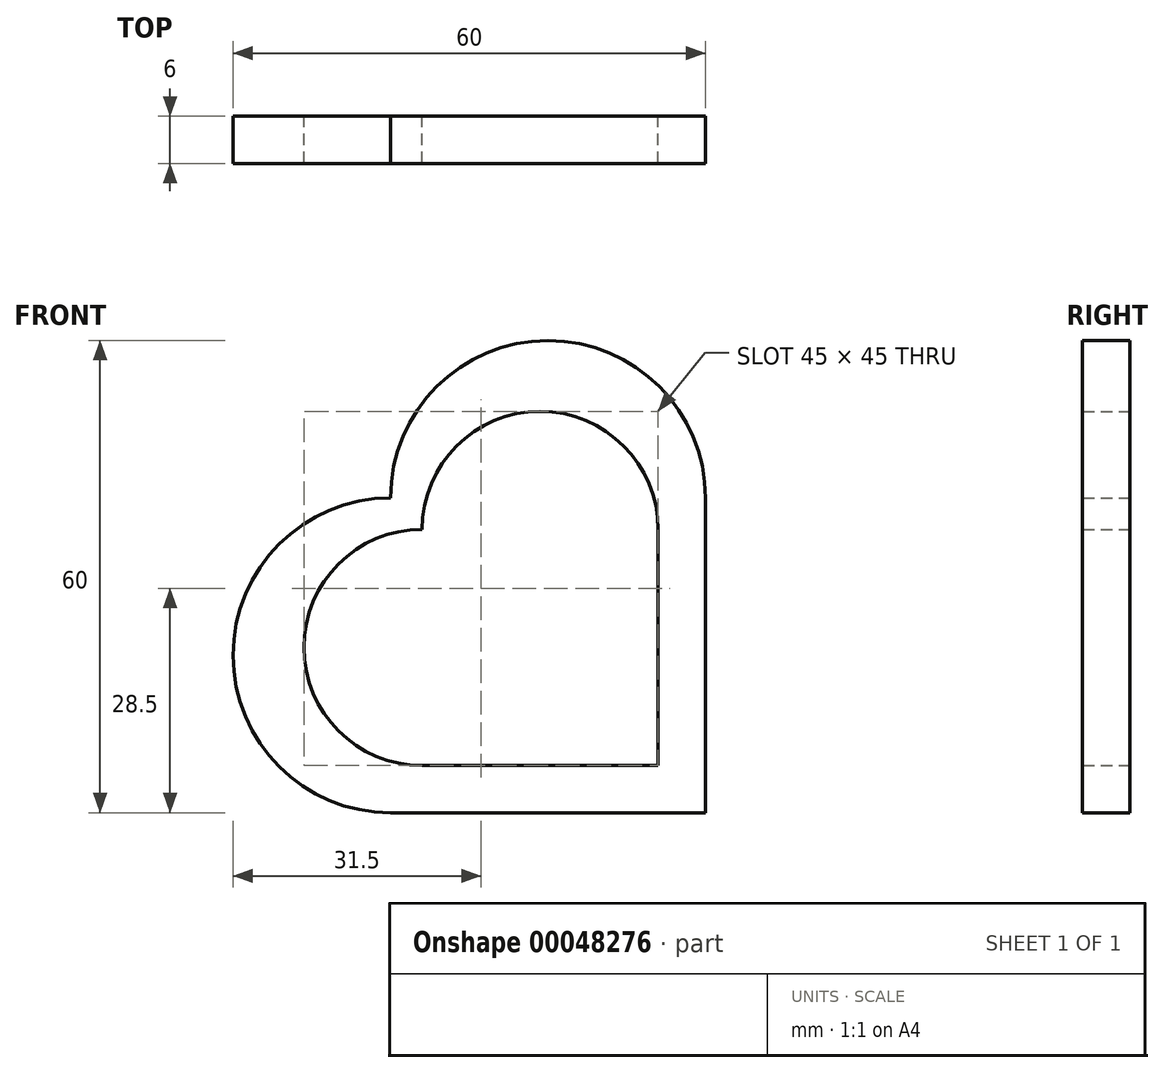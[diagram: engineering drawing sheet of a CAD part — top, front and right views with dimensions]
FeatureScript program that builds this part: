
annotation { "Feature Type Name" : "Feature", "Feature Type Description" : "" }
export const myFeature = defineFeature(function(context is Context, id is Id, definition is map)
    precondition{}
    {
        {
            var Q0;
            Q0=qCreatedBy(makeId("Front.planeOp"),FACE);
            var sketch = newSketch(context, id + "F0", { "sketchPlane" : qUnion([Q0])});
            skLineSegment(sketch, "E0", {"start": v(0, 0) * mm, "end": v(-40, 0) * mm});
            skLineSegment(sketch, "E1", {"start": v(0, 40) * mm, "end": v(0, 0) * mm});
            skArc(sketch, "E2", {"start": v(-40, 40) * mm, "mid": v(-60, 20) * mm, "end": v(-40, 0) * mm});
            skArc(sketch, "E3", {"start": v(0, 40) * mm, "mid": v(-20, 60) * mm, "end": v(-40, 40) * mm});
            skLineSegment(sketch, "E4", {"start": v(-36, 6) * mm, "end": v(-6, 6) * mm});
            skLineSegment(sketch, "E5", {"start": v(-6, 6) * mm, "end": v(-6, 36) * mm});
            skLineSegment(sketch, "E6", {"start": v(-36, 6) * mm, "end": v(-36, 36) * mm, "construction": true});
            skLineSegment(sketch, "E7", {"start": v(-36, 36) * mm, "end": v(-6, 36) * mm, "construction": true});
            skPoint(sketch, "E8", {"position": v(-36, 21) * mm});
            skPoint(sketch, "E9", {"position": v(-21, 36) * mm});
            skArc(sketch, "E10", {"start": v(-36, 6) * mm, "mid": v(-51, 21) * mm, "end": v(-36, 36) * mm});
            skArc(sketch, "E11", {"start": v(-36, 36) * mm, "mid": v(-21, 51) * mm, "end": v(-6, 36) * mm});
            skSolve(sketch);
        }
        {
            var Q0;
            Q0=makeQuery(id+"F0.imprint","IMPRINT",FACE,{"disambiguationData":[TD([[makeQuery(id+"F0.imprint","IMPRINT",EDGE,{"derivedFrom":sQuery(id+"F0.wireOp",EDGE,"E0")}),-1.0]])]});
            var Q1;
            Q1 = qSketchRegion(id + "F0", true);
            extrude(context, id + "F1", {"entities" : qUnion([Q0, Q1]), "depth" : 6 * mm});
        }
    });
